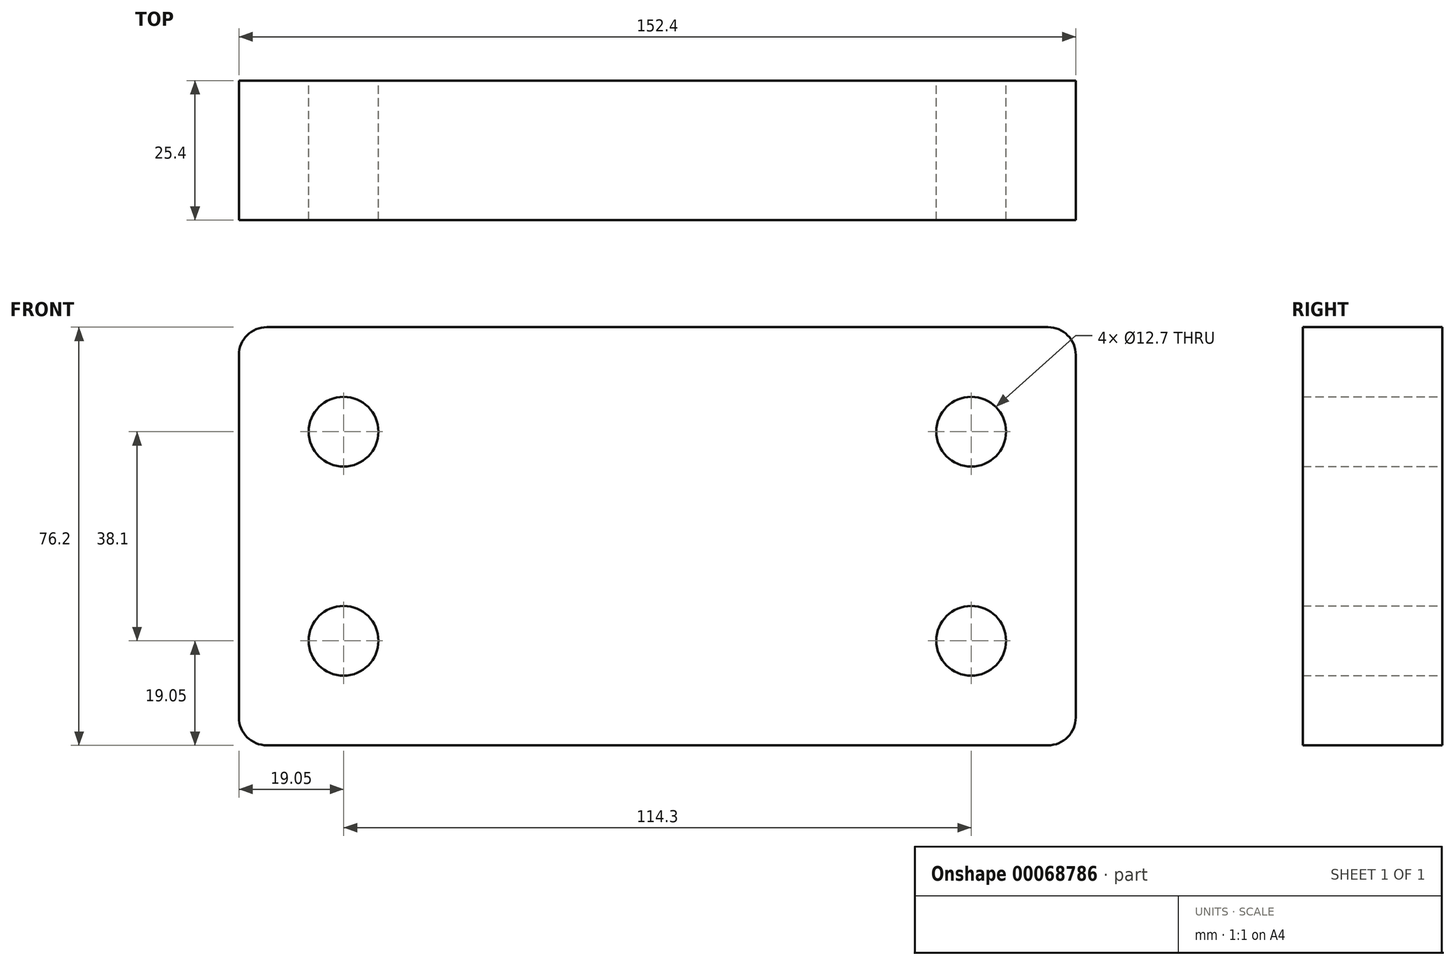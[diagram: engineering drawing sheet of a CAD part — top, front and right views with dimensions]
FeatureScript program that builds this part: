
annotation { "Feature Type Name" : "Feature", "Feature Type Description" : "" }
export const myFeature = defineFeature(function(context is Context, id is Id, definition is map)
    precondition{}
    {
        {
            var Q0;
            Q0=qCreatedBy(makeId("Front.planeOp"),FACE);
            var sketch = newSketch(context, id + "F0", { "sketchPlane" : qUnion([Q0])});
            skLineSegment(sketch, "E0", {"start": v(-76.2, 38.1) * mm, "end": v(76.2, 38.1) * mm});
            skLineSegment(sketch, "E1", {"start": v(76.2, 38.1) * mm, "end": v(76.2, -38.1) * mm});
            skLineSegment(sketch, "E2", {"start": v(-76.2, 38.1) * mm, "end": v(-76.2, -38.1) * mm});
            skLineSegment(sketch, "E3", {"start": v(-76.2, -38.1) * mm, "end": v(76.2, -38.1) * mm});
            skLineSegment(sketch, "E4", {"start": v(-76.2, 0) * mm, "end": v(76.2, 0) * mm, "construction": true});
            skLineSegment(sketch, "E5", {"start": v(0, -38.1) * mm, "end": v(0, 38.1) * mm, "construction": true});
            skCircle(sketch, "E6", {"center": v(-57.15, 19.05) * mm, "radius": 6.35 * mm});
            skCircle(sketch, "E7.MirrorC", {"center": v(-57.15, -19.05) * mm, "radius": 6.35 * mm});
            skCircle(sketch, "E8.MirrorC", {"center": v(57.15, 19.05) * mm, "radius": 6.35 * mm});
            skLineSegment(sketch, "E9.MirrorCS", {"start": v(76.2, 0) * mm, "end": v(-76.2, 0) * mm, "construction": true});
            skCircle(sketch, "E10.MirrorC", {"center": v(57.15, -19.05) * mm, "radius": 6.35 * mm});
            skSolve(sketch);
        }
        {
            var Q0;
            Q0 = qSketchRegion(id + "F0", true);
            extrude(context, id + "F1", {"entities" : qUnion([Q0]), "depth" : 25.4 * mm});
        }
        {
            var Q0;
            Q0=makeQuery(id+"F1.opExtrude","SWEPT_EDGE",EDGE,{"disambiguationData":[OSD([sQuery(id+"F0.wireOp",EDGE,"E0"),sQuery(id+"F0.wireOp",EDGE,"E1")])]});
            var Q1;
            Q1=makeQuery(id+"F1.opExtrude","SWEPT_EDGE",EDGE,{"disambiguationData":[OSD([sQuery(id+"F0.wireOp",EDGE,"E2"),sQuery(id+"F0.wireOp",EDGE,"E3")])]});
            var Q2;
            Q2=makeQuery(id+"F1.opExtrude","SWEPT_EDGE",EDGE,{"disambiguationData":[OSD([sQuery(id+"F0.wireOp",EDGE,"E0"),sQuery(id+"F0.wireOp",EDGE,"E2")])]});
            var Q3;
            Q3=makeQuery(id+"F1.opExtrude","SWEPT_EDGE",EDGE,{"disambiguationData":[OSD([sQuery(id+"F0.wireOp",EDGE,"E1"),sQuery(id+"F0.wireOp",EDGE,"E3")])]});
            fillet(context, id + "F2", {"entities" : qUnion([Q0, Q1, Q2, Q3]), "radius" : 5.08 * mm, "tangentPropagation" : true, "allowEdgeOverflow" : false});
        }
    });
